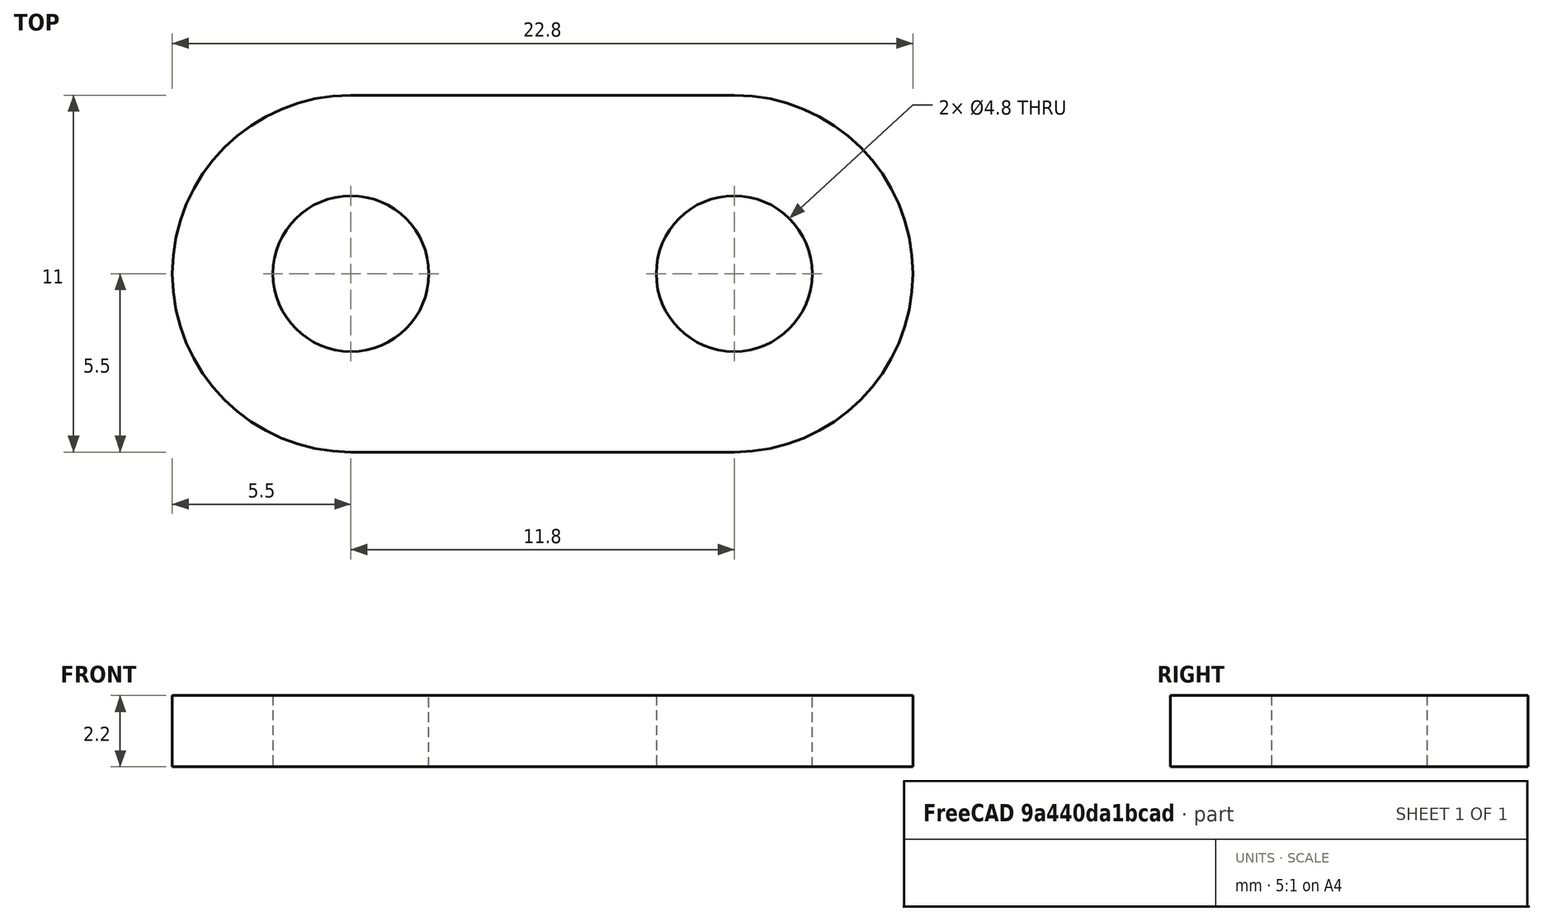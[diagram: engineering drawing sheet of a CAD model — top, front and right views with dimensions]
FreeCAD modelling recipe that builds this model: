
FCSTD DOCUMENT  (FreeCAD 0.21R33668 +26 (Git))
Label: Door Latch Cam Rod
License: All rights reserved
LicenseURL: http://en.wikipedia.org/wiki/All_rights_reserved
objects: Sketcher::SketchObject×1, PartDesign::Pad×1, PartDesign::Body×1
note: 4 computed .brp shape members not serialized (recipe doc carries the construction recipe); baked Part::Feature solids carry a one-line shape summary decoded from their .brp

FEATURE [Sketcher::SketchObject] Sketch
  FullyConstrained = true
  MapMode = 5
  Support = -> [XY_Plane]
  sketch-geometry (6):
    g0: Circle CenterX=-5.9 CenterY=0 CenterZ=0 NormalX=0 NormalY=0 NormalZ=1 AngleXU=0 Radius=2.4
    g1: Circle CenterX=5.9 CenterY=0 CenterZ=0 NormalX=0 NormalY=0 NormalZ=1 AngleXU=0 Radius=2.4
    g2: ArcOfCircle CenterX=-5.9 CenterY=0 CenterZ=0 NormalX=0 NormalY=0 NormalZ=1 AngleXU=0 Radius=5.5 StartAngle=1.5708 EndAngle=4.71239
    g3: ArcOfCircle CenterX=5.9 CenterY=0 CenterZ=0 NormalX=0 NormalY=0 NormalZ=1 AngleXU=0 Radius=5.5 StartAngle=4.71239 EndAngle=7.85398
    g4: LineSegment StartX=-5.9 StartY=-5.5 StartZ=0 EndX=5.9 EndY=-5.5 EndZ=0
    g5: LineSegment StartX=5.9 StartY=5.5 StartZ=0 EndX=-5.9 EndY=5.5 EndZ=0
  constraints (13):
    c: PointOnObject(g0,g-1)
    c: Diameter(g0) = 4.8
    c: Diameter(g1) = 4.8
    c: DistanceX(g0,g1) = 11.8
    c: Symmetric(g0,g1,g-1)
    c: Tangent(g2,g4) = -1.5708
    c: Tangent(g4,g3) = -1.5708
    c: Tangent(g3,g5) = -1.5708
    c: Tangent(g5,g2) = -1.5708
    c: Equal(g2,g3)
    c: Coincident(g2,g0)
    c: Coincident(g3,g1)
    c: DistanceY(g2,g2) = 11
FEATURE [PartDesign::Pad] Pad
  Direction = (0,0,1)
  Length = 2.2
  Length2 = 10
  Profile = -> Sketch
  ReferenceAxis = -> Sketch [N_Axis]
  Type = 0
FEATURE [PartDesign::Body] Body
  Group = -> [Sketch,Pad]
  Origin = -> Origin
  Tip = -> Pad
